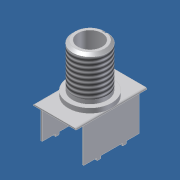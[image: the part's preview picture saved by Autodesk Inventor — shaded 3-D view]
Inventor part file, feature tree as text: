
AUTODESK INVENTOR PART (.ipt)
format: ipt  version: 2014 (Build 180170000, 170)  size: 183,808 bytes
history: native  units: in
note: dims shown in document units (in); Inventor stores cm internally (conversion verified against a paired STEP export)
features: other x35, sketch x5, extrude x3, revolve x2, thread x1
ambient origin geometry x8: Origin, YZ Plane, XZ Plane, XY Plane, X Axis, Y Axis, Z Axis, Center Point
bodies: Solid1 (feature_tree)
feature tree (46):
  extrude  "Extrusion1"  Depth=0.311in TaperAngle=0.0deg
  extrude  "Extrusion2"  Depth=0.285in
  revolve  "Revolution1"  Angle=360.0deg
  thread  "Thread1"  [1 undecoded]
  extrude  "Extrusion3"  [1 undecoded]
  revolve  "Revolution2"  [1 undecoded]
  other  "1_XY"
  other  "1_YZ"
  other  "1_ZX"
  other  "1_X"
  other  "1_Y"
  other  "1_Z"
  other  "1_Center"
  other  "2_XY"
  other  "2_YZ"
  other  "2_ZX"
  other  "2_X"
  other  "2_Y"
  other  "2_Z"
  other  "2_Center"
  other  "3_XY"
  other  "3_YZ"
  other  "3_ZX"
  other  "3_X"
  other  "3_Y"
  other  "3_Z"
  other  "3_Center"
  other  "4_XY"
  other  "4_YZ"
  other  "4_ZX"
  other  "4_X"
  other  "4_Y"
  other  "4_Z"
  other  "4_Center"
  other  "to_base_XY"
  other  "to_base_YZ"
  other  "to_base_ZX"
  other  "to_base_X"
  other  "to_base_Y"
  other  "to_base_Z"
  other  "to_base_Center"
  sketch  "Sketch_1"  dims[d0=0.512in d1=0.0in d2=0.311in d3=0.0in]
  sketch  "Sketch_2"  dims[d7=0.385in d8=0.0in d9=360.0deg]
  sketch  "Sketch_15"
  sketch  "Sketch_8"
  sketch  "Sketch_10_ALT_Drilling_1"  dims[d4=360.0deg d5=0.285in d6=0.03in]
note: 3 required parameter values undecoded (feature->parameter linkage not recoverable at this tier; creation-order binding heuristic only, values carry confidence <= 0.55)
